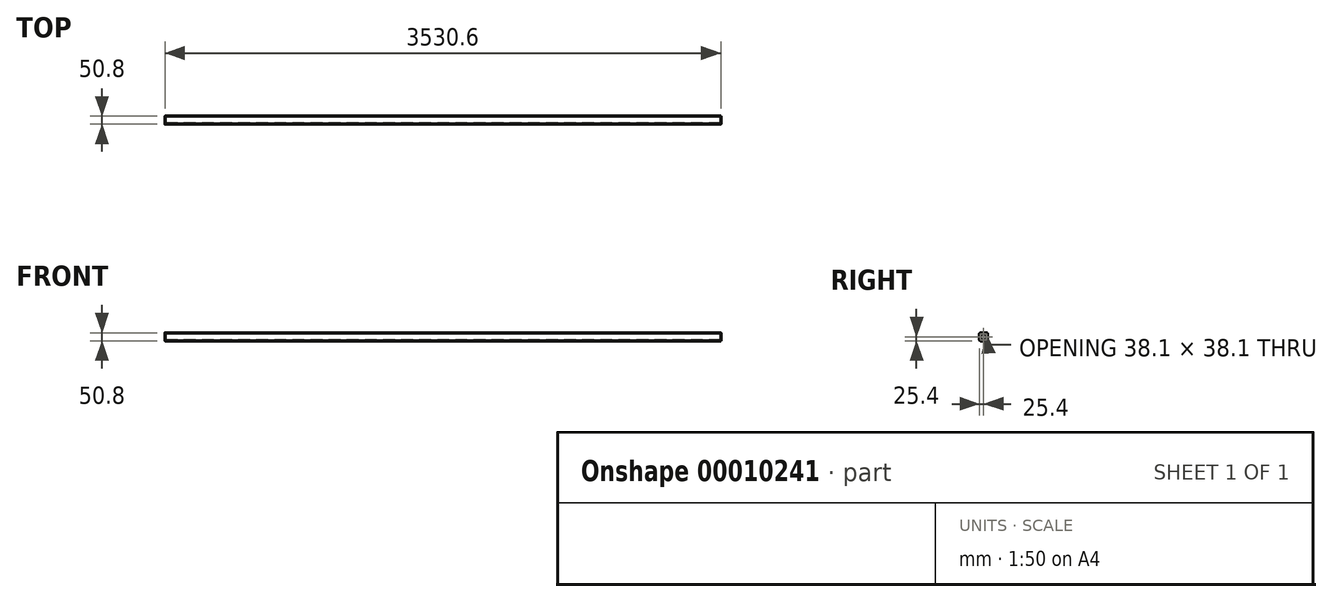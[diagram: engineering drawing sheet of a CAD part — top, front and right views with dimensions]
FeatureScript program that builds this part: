
annotation { "Feature Type Name" : "Feature", "Feature Type Description" : "" }
export const myFeature = defineFeature(function(context is Context, id is Id, definition is map)
    precondition{}
    {
        {
            var Q0;
            Q0=qCreatedBy(makeId("Right.planeOp"),FACE);
            var sketch = newSketch(context, id + "F0", { "sketchPlane" : qUnion([Q0])});
            skLineSegment(sketch, "E0.bottom", {"start": v(6.35, 50.8) * mm, "end": v(44.45, 50.8) * mm});
            skLineSegment(sketch, "E0.top", {"start": v(6.35, 0) * mm, "end": v(44.45, 0) * mm});
            skLineSegment(sketch, "E0.left", {"start": v(0, 44.45) * mm, "end": v(0, 6.35) * mm});
            skLineSegment(sketch, "E0.right", {"start": v(50.8, 44.45) * mm, "end": v(50.8, 6.35) * mm});
            skPoint(sketch, "E1.visualSharp", {"position": v(0, 50.8) * mm});
            skArc(sketch, "E1.filletArc", {"start": v(6.35, 50.8) * mm, "mid": v(1.86, 48.94) * mm, "end": v(0, 44.45) * mm});
            skPoint(sketch, "E2.visualSharp", {"position": v(0, 0) * mm});
            skArc(sketch, "E2.filletArc", {"start": v(0, 6.35) * mm, "mid": v(1.86, 1.86) * mm, "end": v(6.35, 0) * mm});
            skPoint(sketch, "E3.visualSharp", {"position": v(50.8, 0) * mm});
            skArc(sketch, "E3.filletArc", {"start": v(44.45, 0) * mm, "mid": v(48.94, 1.86) * mm, "end": v(50.8, 6.35) * mm});
            skPoint(sketch, "E4.visualSharp", {"position": v(50.8, 50.8) * mm});
            skArc(sketch, "E4.filletArc", {"start": v(50.8, 44.45) * mm, "mid": v(48.94, 48.94) * mm, "end": v(44.45, 50.8) * mm});
            skLineSegment(sketch, "E5", {"start": v(6.35, 38.1) * mm, "end": v(6.35, 12.7) * mm});
            skLineSegment(sketch, "E6", {"start": v(12.7, 6.35) * mm, "end": v(38.1, 6.35) * mm});
            skLineSegment(sketch, "E7", {"start": v(44.45, 12.7) * mm, "end": v(44.45, 38.1) * mm});
            skLineSegment(sketch, "E8", {"start": v(38.1, 44.45) * mm, "end": v(12.7, 44.45) * mm});
            skPoint(sketch, "E9.newPointA", {"position": v(6.35, 38.18) * mm});
            skArc(sketch, "E9.filletArc", {"start": v(12.7, 44.45) * mm, "mid": v(8.2, 42.6) * mm, "end": v(6.35, 38.1) * mm});
            skArc(sketch, "E10.filletArc", {"start": v(44.45, 38.1) * mm, "mid": v(42.6, 42.6) * mm, "end": v(38.1, 44.45) * mm});
            skArc(sketch, "E11.filletArc", {"start": v(38.1, 6.35) * mm, "mid": v(42.6, 8.2) * mm, "end": v(44.45, 12.7) * mm});
            skArc(sketch, "E12.filletArc", {"start": v(6.35, 12.7) * mm, "mid": v(8.2, 8.2) * mm, "end": v(12.7, 6.35) * mm});
            skSolve(sketch);
        }
        {
            var Q0;
            Q0=makeQuery(id+"F0.imprint","IMPRINT",FACE,{"disambiguationData":[TD([[makeQuery(id+"F0.imprint","IMPRINT",EDGE,{"derivedFrom":sQuery(id+"F0.wireOp",EDGE,"E0.bottom")}),-1.0]])]});
            extrude(context, id + "F1", {"entities" : qUnion([Q0]), "depth" : 3530.6 * mm});
        }
    });
